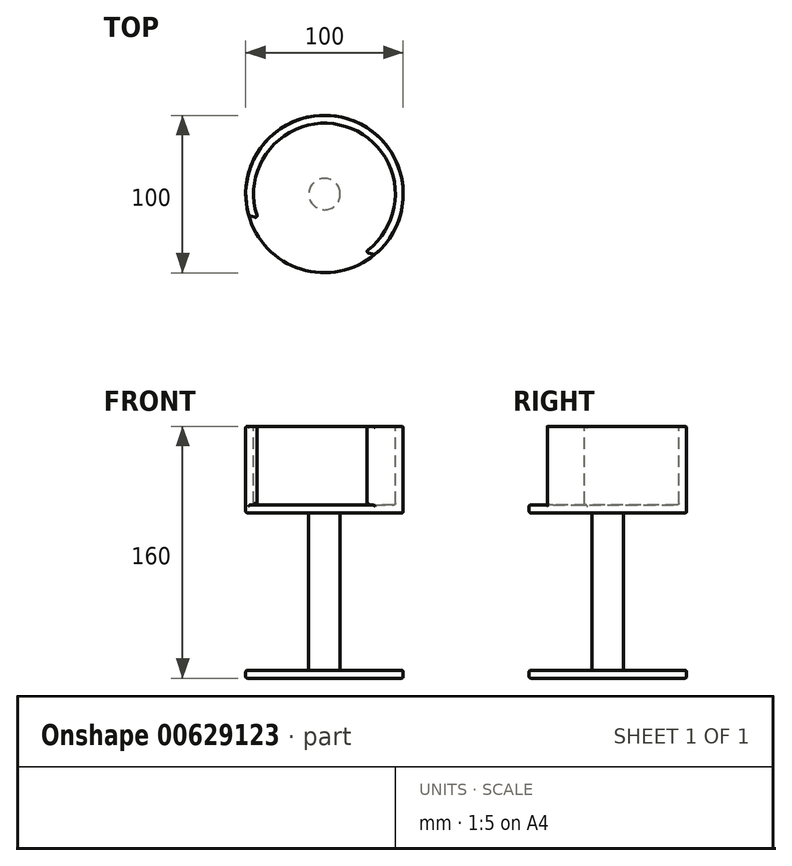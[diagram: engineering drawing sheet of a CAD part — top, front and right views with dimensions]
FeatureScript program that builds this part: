
annotation { "Feature Type Name" : "Feature", "Feature Type Description" : "" }
export const myFeature = defineFeature(function(context is Context, id is Id, definition is map)
    precondition{}
    {
        {
            var Q0;
            Q0=qCreatedBy(makeId("Top.planeOp"),FACE);
            var sketch = newSketch(context, id + "F0", { "sketchPlane" : qUnion([Q0])});
            skCircle(sketch, "E0", {"center": v(0, 0) * mm, "radius": 50 * mm});
            skSolve(sketch);
        }
        {
            var Q0;
            Q0=makeQuery(id+"F0.imprint","IMPRINT",FACE,{"disambiguationData":[TD([[makeQuery(id+"F0.imprint","IMPRINT",EDGE,{"derivedFrom":sQuery(id+"F0.wireOp",EDGE,"E0")}),1.0]])]});
            extrude(context, id + "F1", {"entities" : qUnion([Q0]), "depth" : 5 * mm, "offsetDistance" : 25 * mm});
        }
        {
            var Q0;
            Q0=makeQuery(id+"F1.opExtrude","CAP_FACE",FACE,{"disambiguationData":[OSD([sQuery(id+"F0.wireOp",EDGE,"E0")])],"isStart":false});
            var sketch = newSketch(context, id + "F2", { "sketchPlane" : qUnion([Q0])});
            skCircle(sketch, "E1", {"center": v(0, 0) * mm, "radius": 10 * mm});
            skSolve(sketch);
        }
        {
            var Q0;
            Q0=makeQuery(id+"F2.imprint","IMPRINT",FACE,{"disambiguationData":[TD([[makeQuery(id+"F2.imprint","IMPRINT",EDGE,{"derivedFrom":sQuery(id+"F2.wireOp",EDGE,"E1")}),1.0]])]});
            extrude(context, id + "F3", {"entities" : qUnion([Q0]), "operationType" : NewBodyOperationType.ADD, "depth" : 100 * mm, "offsetDistance" : 25 * mm});
        }
        {
            var Q0;
            Q0=makeQuery(id+"F3.opExtrude","CAP_FACE",FACE,{"disambiguationData":[OSD([sQuery(id+"F2.wireOp",EDGE,"E1")])],"isStart":false});
            cPlane(context, id + "F4", {"entities" : qUnion([Q0]), "cplaneType" : CPlaneType.OFFSET, "offset" : 0 * mm, "width" : 150 * mm, "height" : 150 * mm});
        }
        {
            var Q0;
            Q0=qCreatedBy(id+"F4.planeOp",FACE);
            var sketch = newSketch(context, id + "F5", { "sketchPlane" : qUnion([Q0])});
            skCircle(sketch, "E2", {"center": v(0, 0) * mm, "radius": 50 * mm});
            skSolve(sketch);
        }
        {
            var Q0;
            Q0=makeQuery(id+"F5.imprint","IMPRINT",FACE,{"disambiguationData":[TD([[makeQuery(id+"F5.imprint","IMPRINT",EDGE,{"derivedFrom":sQuery(id+"F5.wireOp",EDGE,"E2")}),1.0]])]});
            extrude(context, id + "F6", {"entities" : qUnion([Q0]), "operationType" : NewBodyOperationType.ADD, "depth" : 5 * mm, "offsetDistance" : 25 * mm});
        }
        {
            var Q0;
            Q0=makeQuery(id+"F6.opExtrude","CAP_FACE",FACE,{"disambiguationData":[OSD([sQuery(id+"F5.wireOp",EDGE,"E2")])],"isStart":false});
            var sketch = newSketch(context, id + "F7", { "sketchPlane" : qUnion([Q0])});
            skArc(sketch, "E3", {"start": v(31.78, -38.6) * mm, "mid": v(15.03, 47.82) * mm, "end": v(-48.15, -13.48) * mm});
            skLineSegment(sketch, "E4", {"start": v(-48.15, -13.48) * mm, "end": v(31.78, -38.6) * mm});
            skSolve(sketch);
        }
        {
            var Q0;
            {var subQ0=sQuery(id+"F7.wireOp",EDGE,"E4");Q0=makeQuery(id+"F7.imprint","IMPRINT",FACE,{"disambiguationData":[TD([[makeQuery(id+"F7.imprint","IMPRINT",EDGE,{"derivedFrom":subQ0}),1.0]])]});}
            extrude(context, id + "F8", {"entities" : qUnion([Q0]), "operationType" : NewBodyOperationType.ADD, "depth" : 50 * mm, "offsetDistance" : 25 * mm});
        }
        {
            var Q0;
            Q0=makeQuery(id+"F8.opExtrude","CAP_FACE",FACE,{"disambiguationData":[OSD([sQuery(id+"F5.wireOp",EDGE,"E2"),sQuery(id+"F7.wireOp",EDGE,"E4")])],"isStart":false});
            var sketch = newSketch(context, id + "F9", { "sketchPlane" : qUnion([Q0])});
            skCircle(sketch, "E5", {"center": v(0, 0) * mm, "radius": 45 * mm});
            skSolve(sketch);
        }
        {
            var Q0;
            Q0 = qSketchRegion(id + "F9", true);
            var Q1;
            Q1=sQuery(id+"F9.wireOp",EDGE,"E5");
            extrude(context, id + "F10", {"entities" : qUnion([Q0]), "operationType" : NewBodyOperationType.REMOVE, "surfaceEntities" : qUnion([Q1]), "oppositeDirection" : true, "depth" : 50 * mm, "offsetDistance" : 25 * mm});
        }
        {
            var Q0;
            {var subQ0=sQuery(id+"F7.wireOp",EDGE,"E4");var subQ1=sQuery(id+"F7.wireOp",EDGE,"E3");var subQ2=sQuery(id+"F5.wireOp",EDGE,"E2");Q0=makeQuery(id+"F8.opExtrude","SWEPT_EDGE",EDGE,{"disambiguationData":[OSD([subQ2,subQ1,subQ0]),TDD([makeQuery(id+"F7.imprint","INTERSECT",VERTEX,{"disambiguationData":[OD(1.0)],"derivedFrom":[makeQuery(id+"F6.opExtrude","CAP_EDGE",EDGE,{"disambiguationData":[OSD([subQ2])],"isStart":false}),subQ1,subQ0]})])]});}
            var Q1;
            {var subQ0=sQuery(id+"F7.wireOp",EDGE,"E4");var subQ1=sQuery(id+"F7.wireOp",EDGE,"E3");var subQ2=sQuery(id+"F5.wireOp",EDGE,"E2");Q1=makeQuery(id+"F8.opExtrude","SWEPT_EDGE",EDGE,{"disambiguationData":[OSD([subQ2,subQ1,subQ0]),TDD([makeQuery(id+"F7.imprint","INTERSECT",VERTEX,{"disambiguationData":[OD(0.0)],"derivedFrom":[makeQuery(id+"F6.opExtrude","CAP_EDGE",EDGE,{"disambiguationData":[OSD([subQ2])],"isStart":false}),subQ1,subQ0]})])]});}
            var Q2;
            Q2=makeQuery(id+"F10.boolean.opBoolean","COPY",EDGE,{"derivedFrom":makeQuery(id+"F10.opExtrude","CAP_EDGE",EDGE,{"disambiguationData":[OSD([sQuery(id+"F9.wireOp",EDGE,"E5")])],"isStart":true})});
            var Q3;
            Q3=makeQuery(id+"F8.opExtrude","CAP_EDGE",EDGE,{"disambiguationData":[OSD([sQuery(id+"F5.wireOp",EDGE,"E2")])],"isStart":false});
            var Q4;
            Q4=makeQuery(id+"F6.opExtrude","CAP_EDGE",EDGE,{"disambiguationData":[OSD([sQuery(id+"F5.wireOp",EDGE,"E2")])],"isStart":false});
            var Q5;
            Q5=makeQuery(id+"F10.boolean.opBoolean","INTERSECT",EDGE,{"disambiguationData":[OD(1.0)],"derivedFrom":[makeQuery(id+"F8.opExtrude","SWEPT_FACE",FACE,{"disambiguationData":[OSD([sQuery(id+"F7.wireOp",EDGE,"E4")])]}),makeQuery(id+"F10.opExtrude","SWEPT_FACE",FACE,{"disambiguationData":[OSD([sQuery(id+"F9.wireOp",EDGE,"E5")])]})]});
            var Q6;
            Q6=makeQuery(id+"F10.boolean.opBoolean","INTERSECT",EDGE,{"disambiguationData":[OD(0.0)],"derivedFrom":[makeQuery(id+"F8.opExtrude","SWEPT_FACE",FACE,{"disambiguationData":[OSD([sQuery(id+"F7.wireOp",EDGE,"E4")])]}),makeQuery(id+"F10.opExtrude","SWEPT_FACE",FACE,{"disambiguationData":[OSD([sQuery(id+"F9.wireOp",EDGE,"E5")])]})]});
            var Q7;
            Q7=makeQuery(id+"F6.opExtrude","CAP_EDGE",EDGE,{"disambiguationData":[OSD([sQuery(id+"F5.wireOp",EDGE,"E2")])],"isStart":true});
            var Q8;
            Q8=makeQuery(id+"F3.opExtrude","CAP_EDGE",EDGE,{"disambiguationData":[OSD([sQuery(id+"F2.wireOp",EDGE,"E1")])],"isStart":false});
            var Q9;
            Q9=makeQuery(id+"F3.opExtrude","CAP_EDGE",EDGE,{"disambiguationData":[OSD([sQuery(id+"F2.wireOp",EDGE,"E1")])],"isStart":true});
            var Q10;
            Q10=makeQuery(id+"F1.opExtrude","CAP_EDGE",EDGE,{"disambiguationData":[OSD([sQuery(id+"F0.wireOp",EDGE,"E0")])],"isStart":false});
            var Q11;
            Q11=makeQuery(id+"F1.opExtrude","CAP_EDGE",EDGE,{"disambiguationData":[OSD([sQuery(id+"F0.wireOp",EDGE,"E0")])],"isStart":true});
            var Q12;
            Q12=makeQuery(id+"F3.opExtrude","SWEPT_FACE",FACE,{"disambiguationData":[OSD([sQuery(id+"F2.wireOp",EDGE,"E1")])]});
            var Q13;
            Q13=makeQuery(id+"F10.boolean.opBoolean","COPY",EDGE,{"derivedFrom":makeQuery(id+"F10.opExtrude","CAP_EDGE",EDGE,{"disambiguationData":[OSD([sQuery(id+"F9.wireOp",EDGE,"E5")])],"isStart":false})});
            fillet(context, id + "F11", {"entities" : qUnion([Q0, Q1, Q2, Q3, Q4, Q5, Q6, Q7, Q8, Q9, Q10, Q11, Q12, Q13]), "radius" : 1 * mm, "tangentPropagation" : true, "allowEdgeOverflow" : false});
        }
    });
